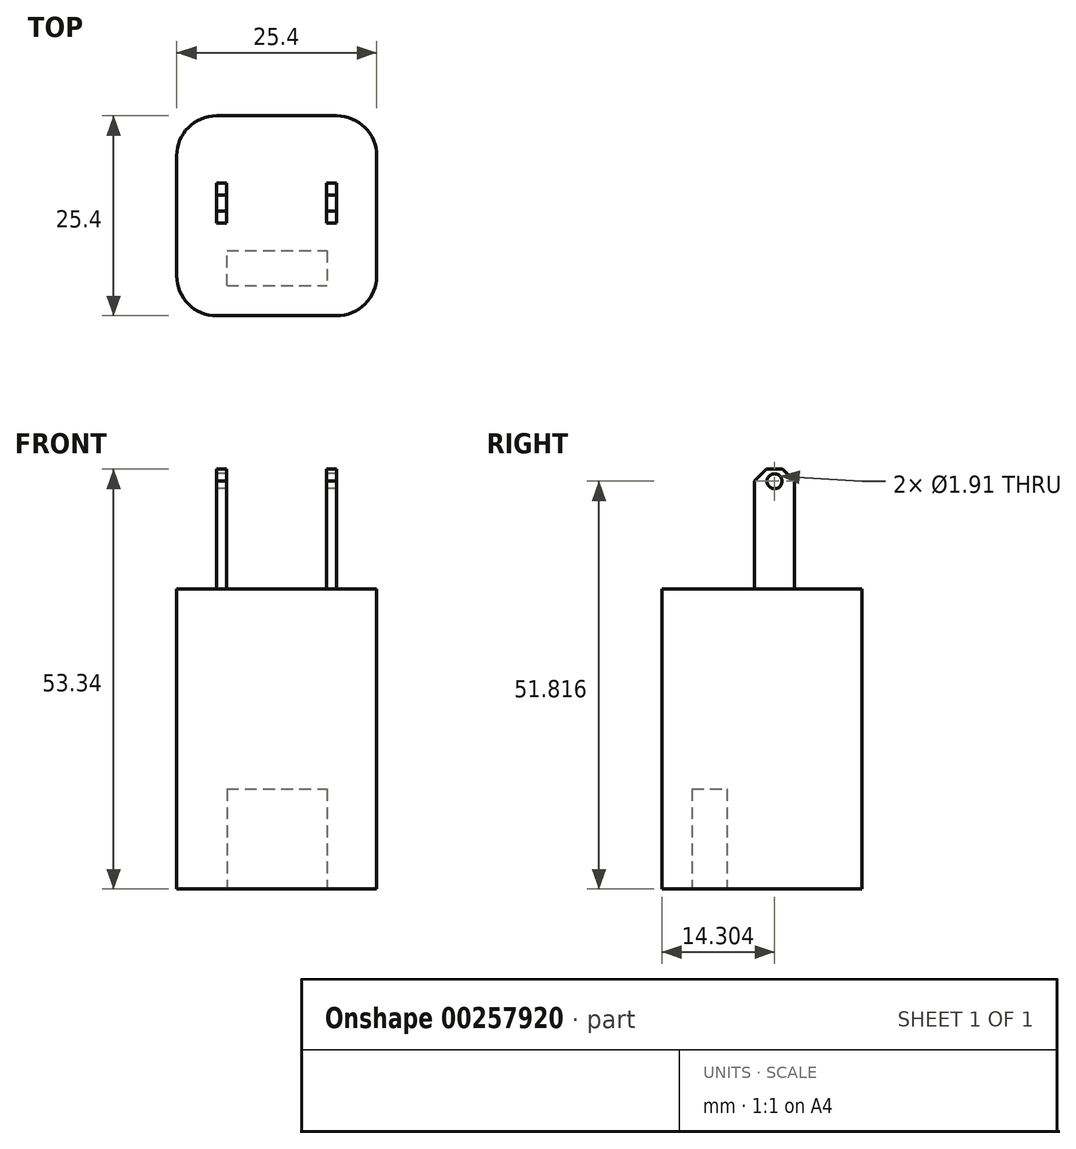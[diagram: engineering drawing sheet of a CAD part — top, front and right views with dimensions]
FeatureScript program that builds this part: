
annotation { "Feature Type Name" : "Feature", "Feature Type Description" : "" }
export const myFeature = defineFeature(function(context is Context, id is Id, definition is map)
    precondition{}
    {
        {
            var Q0;
            Q0=qCreatedBy(makeId("Top.planeOp"),FACE);
            var sketch = newSketch(context, id + "F0", { "sketchPlane" : qUnion([Q0])});
            skLineSegment(sketch, "E0", {"start": v(0, -25.4) * mm, "end": v(-12.7, -25.4) * mm});
            skLineSegment(sketch, "E1", {"start": v(-12.7, -25.4) * mm, "end": v(-12.7, 0) * mm});
            skLineSegment(sketch, "E2", {"start": v(-12.7, 0) * mm, "end": v(12.7, 0) * mm});
            skLineSegment(sketch, "E3", {"start": v(12.7, 0) * mm, "end": v(12.7, -25.4) * mm});
            skLineSegment(sketch, "E4", {"start": v(12.7, -25.4) * mm, "end": v(0, -25.4) * mm});
            skLineSegment(sketch, "E5", {"start": v(0.02, -21.59) * mm, "end": v(-6.33, -21.59) * mm});
            skLineSegment(sketch, "E6", {"start": v(-6.33, -21.59) * mm, "end": v(-6.33, -17.14) * mm});
            skLineSegment(sketch, "E7", {"start": v(-6.33, -17.14) * mm, "end": v(6.37, -17.14) * mm});
            skLineSegment(sketch, "E8", {"start": v(6.37, -17.14) * mm, "end": v(6.37, -21.59) * mm});
            skLineSegment(sketch, "E9", {"start": v(0.02, -21.59) * mm, "end": v(6.37, -21.59) * mm});
            skSolve(sketch);
        }
        {
            var Q0;
            Q0=makeQuery(id+"F0.imprint","IMPRINT",FACE,{"disambiguationData":[TD([[makeQuery(id+"F0.imprint","IMPRINT",EDGE,{"derivedFrom":sQuery(id+"F0.wireOp",EDGE,"E0")}),-1.0]])]});
            extrude(context, id + "F1", {"entities" : qUnion([Q0]), "depth" : 12.7 * mm});
        }
        {
            var Q0;
            Q0=makeQuery(id+"F1.opExtrude","CAP_FACE",FACE,{"disambiguationData":[OSD([sQuery(id+"F0.wireOp",EDGE,"E0"),sQuery(id+"F0.wireOp",EDGE,"E1"),sQuery(id+"F0.wireOp",EDGE,"E2"),sQuery(id+"F0.wireOp",EDGE,"E3"),sQuery(id+"F0.wireOp",EDGE,"E4"),sQuery(id+"F0.wireOp",EDGE,"E5"),sQuery(id+"F0.wireOp",EDGE,"E6"),sQuery(id+"F0.wireOp",EDGE,"E7"),sQuery(id+"F0.wireOp",EDGE,"E8"),sQuery(id+"F0.wireOp",EDGE,"E9")])],"isStart":false});
            var sketch = newSketch(context, id + "F2", { "sketchPlane" : qUnion([Q0])});
            skLineSegment(sketch, "E10", {"start": v(-12.7, 0) * mm, "end": v(-12.7, -25.4) * mm});
            skLineSegment(sketch, "E11", {"start": v(-12.7, -25.4) * mm, "end": v(12.7, -25.4) * mm});
            skLineSegment(sketch, "E12", {"start": v(12.7, -25.4) * mm, "end": v(12.7, 0) * mm});
            skLineSegment(sketch, "E13", {"start": v(12.7, 0) * mm, "end": v(-12.7, 0) * mm});
            skSolve(sketch);
        }
        {
            var Q0;
            Q0 = qSketchRegion(id + "F2", true);
            extrude(context, id + "F3", {"entities" : qUnion([Q0]), "operationType" : NewBodyOperationType.ADD, "depth" : 25.4 * mm});
        }
        {
            var Q0;
            Q0=makeQuery(id+"F3.boolean.opBoolean","MERGE",EDGE,{"derivedFrom":[makeQuery(id+"F1.opExtrude","SWEPT_EDGE",EDGE,{"disambiguationData":[OSD([sQuery(id+"F0.wireOp",EDGE,"E0"),sQuery(id+"F0.wireOp",EDGE,"E1")])]}),makeQuery(id+"F3.opExtrude","SWEPT_EDGE",EDGE,{"disambiguationData":[OSD([sQuery(id+"F2.wireOp",EDGE,"E10"),sQuery(id+"F2.wireOp",EDGE,"E11")])]})]});
            var Q1;
            Q1=makeQuery(id+"F3.boolean.opBoolean","MERGE",EDGE,{"derivedFrom":[makeQuery(id+"F1.opExtrude","SWEPT_EDGE",EDGE,{"disambiguationData":[OSD([sQuery(id+"F0.wireOp",EDGE,"E3"),sQuery(id+"F0.wireOp",EDGE,"E4")])]}),makeQuery(id+"F3.opExtrude","SWEPT_EDGE",EDGE,{"disambiguationData":[OSD([sQuery(id+"F2.wireOp",EDGE,"E11"),sQuery(id+"F2.wireOp",EDGE,"E12")])]})]});
            var Q2;
            Q2=makeQuery(id+"F3.boolean.opBoolean","MERGE",EDGE,{"derivedFrom":[makeQuery(id+"F1.opExtrude","SWEPT_EDGE",EDGE,{"disambiguationData":[OSD([sQuery(id+"F0.wireOp",EDGE,"E1"),sQuery(id+"F0.wireOp",EDGE,"E2")])]}),makeQuery(id+"F3.opExtrude","SWEPT_EDGE",EDGE,{"disambiguationData":[OSD([sQuery(id+"F2.wireOp",EDGE,"E10"),sQuery(id+"F2.wireOp",EDGE,"E13")])]})]});
            var Q3;
            Q3=makeQuery(id+"F3.boolean.opBoolean","MERGE",EDGE,{"derivedFrom":[makeQuery(id+"F1.opExtrude","SWEPT_EDGE",EDGE,{"disambiguationData":[OSD([sQuery(id+"F0.wireOp",EDGE,"E2"),sQuery(id+"F0.wireOp",EDGE,"E3")])]}),makeQuery(id+"F3.opExtrude","SWEPT_EDGE",EDGE,{"disambiguationData":[OSD([sQuery(id+"F2.wireOp",EDGE,"E12"),sQuery(id+"F2.wireOp",EDGE,"E13")])]})]});
            fillet(context, id + "F4", {"entities" : qUnion([Q0, Q1, Q2, Q3]), "radius" : 5.08 * mm, "tangentPropagation" : true, "allowEdgeOverflow" : false});
        }
        {
            var Q0;
            Q0=makeQuery(id+"F3.opExtrude","CAP_FACE",FACE,{"disambiguationData":[OSD([sQuery(id+"F2.wireOp",EDGE,"E10"),sQuery(id+"F2.wireOp",EDGE,"E11"),sQuery(id+"F2.wireOp",EDGE,"E12"),sQuery(id+"F2.wireOp",EDGE,"E13")])],"isStart":false});
            var sketch = newSketch(context, id + "F5", { "sketchPlane" : qUnion([Q0])});
            skLineSegment(sketch, "E14", {"start": v(-7.62, -13.64) * mm, "end": v(-6.35, -13.64) * mm});
            skLineSegment(sketch, "E15", {"start": v(-6.35, -13.64) * mm, "end": v(-6.35, -8.56) * mm});
            skPoint(sketch, "E16.start.orphan", {"position": v(-7.62, -8.56) * mm});
            skLineSegment(sketch, "E17", {"start": v(-6.35, -8.56) * mm, "end": v(-7.62, -8.56) * mm});
            skLineSegment(sketch, "E18", {"start": v(-7.62, -13.64) * mm, "end": v(-7.62, -8.56) * mm});
            skLineSegment(sketch, "E19", {"start": v(0, 0) * mm, "end": v(0, -25.4) * mm, "construction": true});
            skLineSegment(sketch, "E20.MirrorCS", {"start": v(6.35, -13.64) * mm, "end": v(6.35, -8.56) * mm});
            skLineSegment(sketch, "E21.MirrorCS", {"start": v(7.62, -13.64) * mm, "end": v(7.62, -8.56) * mm});
            skLineSegment(sketch, "E22.MirrorCS", {"start": v(7.62, -13.64) * mm, "end": v(6.35, -13.64) * mm});
            skLineSegment(sketch, "E23.MirrorCS", {"start": v(6.35, -8.56) * mm, "end": v(7.62, -8.56) * mm});
            skSolve(sketch);
        }
        {
            var Q0;
            Q0 = qSketchRegion(id + "F5", true);
            extrude(context, id + "F6", {"entities" : qUnion([Q0]), "operationType" : NewBodyOperationType.ADD, "depth" : 15.24 * mm});
        }
        {
            var Q0;
            Q0=makeQuery(id+"F6.opExtrude","CAP_EDGE",EDGE,{"disambiguationData":[OSD([sQuery(id+"F5.wireOp",EDGE,"E14")])],"isStart":false});
            var Q1;
            Q1=makeQuery(id+"F6.opExtrude","CAP_EDGE",EDGE,{"disambiguationData":[OSD([sQuery(id+"F5.wireOp",EDGE,"E22.MirrorCS")])],"isStart":false});
            var Q2;
            Q2=makeQuery(id+"F6.opExtrude","CAP_EDGE",EDGE,{"disambiguationData":[OSD([sQuery(id+"F5.wireOp",EDGE,"E17")])],"isStart":false});
            var Q3;
            Q3=makeQuery(id+"F6.opExtrude","CAP_EDGE",EDGE,{"disambiguationData":[OSD([sQuery(id+"F5.wireOp",EDGE,"E23.MirrorCS")])],"isStart":false});
            chamfer(context, id + "F7", {"entities" : qUnion([Q0, Q1, Q2, Q3]), "width" : 1.52 * mm, "tangentPropagation" : true});
        }
        {
            var Q0;
            Q0=makeQuery(id+"F6.opExtrude","SWEPT_FACE",FACE,{"disambiguationData":[OSD([sQuery(id+"F5.wireOp",EDGE,"E18")])]});
            var sketch = newSketch(context, id + "F8", { "sketchPlane" : qUnion([Q0])});
            skCircle(sketch, "E24", {"center": v(11.1, 51.82) * mm, "radius": 0.95 * mm});
            skPoint(sketch, "E24.centerSnap0", {"position": v(11.1, 53.34) * mm});
            skSolve(sketch);
        }
        {
            var Q0;
            Q0 = qSketchRegion(id + "F8", true);
            extrude(context, id + "F9", {"entities" : qUnion([Q0]), "operationType" : NewBodyOperationType.REMOVE, "oppositeDirection" : true, "depth" : 127 * mm});
        }
    });
